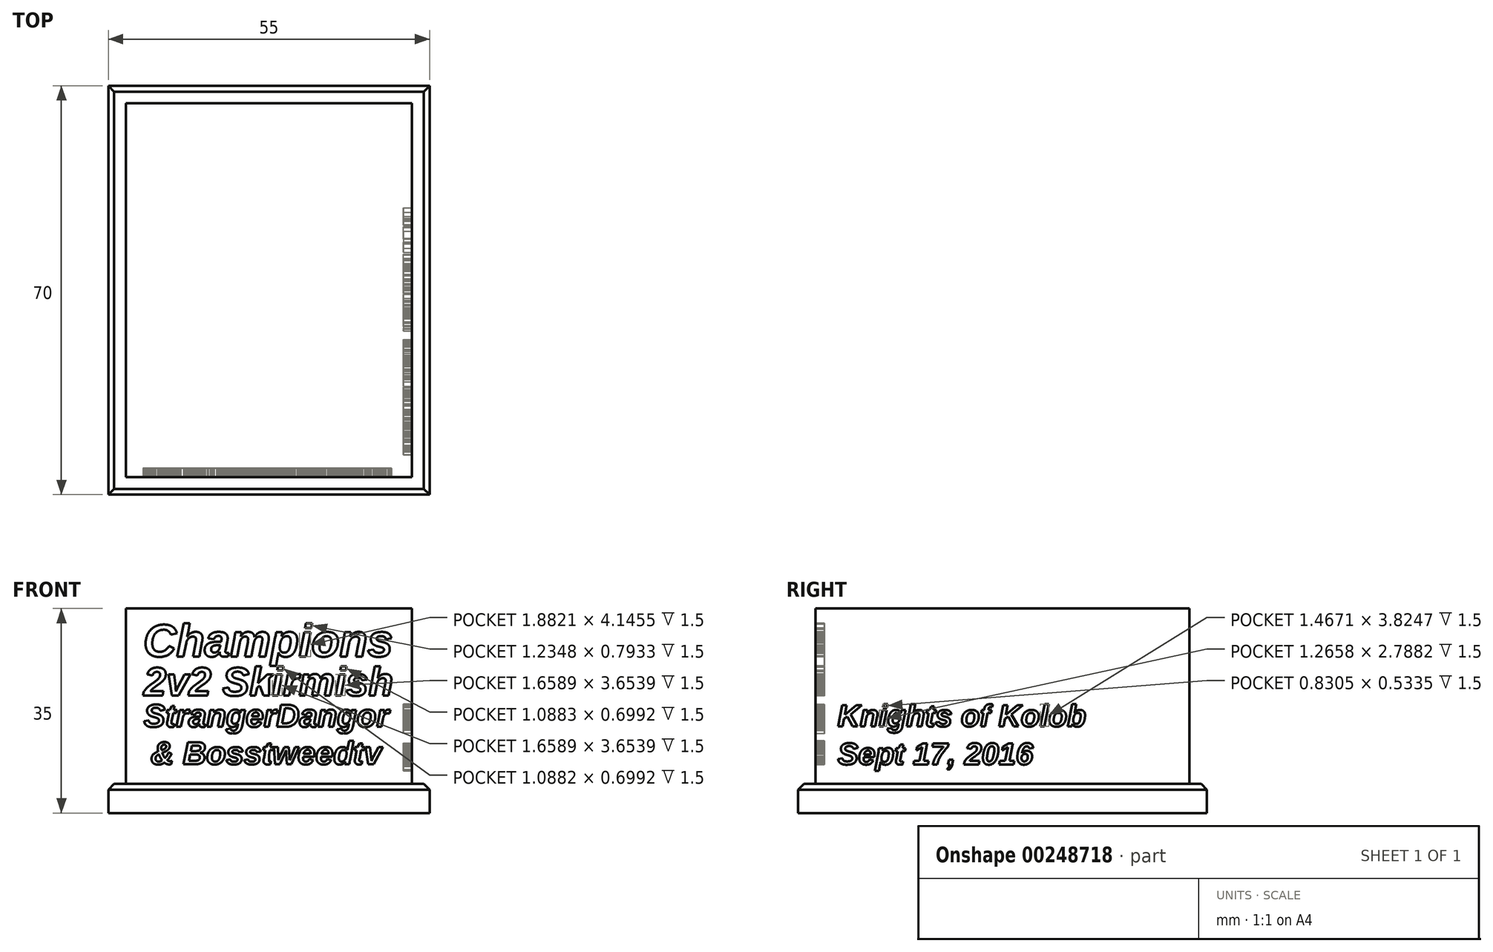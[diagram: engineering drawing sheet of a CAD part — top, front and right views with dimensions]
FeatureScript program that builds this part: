
annotation { "Feature Type Name" : "Feature", "Feature Type Description" : "" }
export const myFeature = defineFeature(function(context is Context, id is Id, definition is map)
    precondition{}
    {
        {
            var Q0;
            Q0=qCreatedBy(makeId("Top.planeOp"),FACE);
            var sketch = newSketch(context, id + "F0", { "sketchPlane" : qUnion([Q0])});
            skLineSegment(sketch, "E0.bottom", {"start": v(0, 0) * mm, "end": v(55, 0) * mm});
            skLineSegment(sketch, "E0.top", {"start": v(0, 70) * mm, "end": v(55, 70) * mm});
            skLineSegment(sketch, "E0.left", {"start": v(0, 0) * mm, "end": v(0, 70) * mm});
            skLineSegment(sketch, "E0.right", {"start": v(55, 0) * mm, "end": v(55, 70) * mm});
            skSolve(sketch);
        }
        {
            var Q0;
            Q0=makeQuery(id+"F0.imprint","IMPRINT",FACE,{"disambiguationData":[TD([[makeQuery(id+"F0.imprint","IMPRINT",EDGE,{"derivedFrom":sQuery(id+"F0.wireOp",EDGE,"E0.bottom")}),1.0]])]});
            extrude(context, id + "F1", {"entities" : qUnion([Q0]), "depth" : 5 * mm});
        }
        {
            var Q0;
            Q0=makeQuery(id+"F1.opExtrude","CAP_FACE",FACE,{"disambiguationData":[OSD([sQuery(id+"F0.wireOp",EDGE,"E0.bottom"),sQuery(id+"F0.wireOp",EDGE,"E0.top"),sQuery(id+"F0.wireOp",EDGE,"E0.left"),sQuery(id+"F0.wireOp",EDGE,"E0.right")])],"isStart":false});
            var sketch = newSketch(context, id + "F2", { "sketchPlane" : qUnion([Q0])});
            skLineSegment(sketch, "E1", {"start": v(0, 0) * mm, "end": v(3, 0) * mm});
            skLineSegment(sketch, "E2", {"start": v(3, 0) * mm, "end": v(3, 3) * mm});
            skLineSegment(sketch, "E3.bottom", {"start": v(3, 3) * mm, "end": v(52, 3) * mm});
            skLineSegment(sketch, "E3.top", {"start": v(3, 67) * mm, "end": v(52, 67) * mm});
            skLineSegment(sketch, "E3.left", {"start": v(3, 3) * mm, "end": v(3, 67) * mm});
            skLineSegment(sketch, "E3.right", {"start": v(52, 3) * mm, "end": v(52, 67) * mm});
            skSolve(sketch);
        }
        {
            var Q0;
            Q0 = qSketchRegion(id + "F2", true);
            var Q1;
            Q1=makeQuery(id+"F2.imprint","IMPRINT",FACE,{"disambiguationData":[TD([[makeQuery(id+"F2.imprint","IMPRINT",EDGE,{"derivedFrom":sQuery(id+"F2.wireOp",EDGE,"E3.bottom")}),1.0]])]});
            extrude(context, id + "F3", {"entities" : qUnion([Q0, Q1]), "operationType" : NewBodyOperationType.ADD, "depth" : 30 * mm});
        }
        {
            var Q0;
            Q0=makeQuery(id+"F3.opExtrude","SWEPT_FACE",FACE,{"disambiguationData":[OSD([sQuery(id+"F2.wireOp",EDGE,"E3.bottom")])]});
            var sketch = newSketch(context, id + "F4", { "sketchPlane" : qUnion([Q0])});
            skLineSegment(sketch, "E4", {"start": v(27.5, 35) * mm, "end": v(27.5, 5) * mm});
            skText(sketch, "E5", { "text": "StrangerDangor", "fontName": "Arimo-BoldItalic.ttf"});
            skText(sketch, "E6", { "text": "& Bosstweedtv", "fontName": "Arimo-BoldItalic.ttf"});
            skText(sketch, "E7", { "text": "Champions", "fontName": "Arimo-BoldItalic.ttf"});
            skText(sketch, "E8", { "text": "2v2 Skirmish", "fontName": "Arimo-BoldItalic.ttf"});
            const initialGuessF4  = {"E5": [0.00607, 0.01474, 1, 0, 0.00397], "E6": [0.00727, 0.00834, 1, 0, 0.00397], "E7": [0.006, 0.02679, 1, 0, 0.00565], "E8": [0.00607, 0.02008, 1, 0, 0.00498]};
            skSetInitialGuess(sketch, initialGuessF4);
            skSolve(sketch);
        }
        {
            var Q0;
            Q0=makeQuery(id+"F3.opExtrude","SWEPT_FACE",FACE,{"disambiguationData":[OSD([sQuery(id+"F2.wireOp",EDGE,"E3.right")])]});
            var sketch = newSketch(context, id + "F5", { "sketchPlane" : qUnion([Q0])});
            skText(sketch, "E9", { "text": "Sept 17, 2016", "fontName": "Arimo-BoldItalic.ttf"});
            skText(sketch, "E10", { "text": "Knights of Kolob", "fontName": "Arimo-BoldItalic.ttf"});
            const initialGuessF5  = {"E9": [0.00678, 0.00831, 1, 0, 0.0038], "E10": [0.00678, 0.01481, 1, 0, 0.0038]};
            skSetInitialGuess(sketch, initialGuessF5);
            skSolve(sketch);
        }
        {
            var Q0;
            Q0=makeQuery(id+"F1.opExtrude","CAP_EDGE",EDGE,{"disambiguationData":[OSD([sQuery(id+"F0.wireOp",EDGE,"E0.bottom")])],"isStart":false});
            var Q1;
            Q1=makeQuery(id+"F1.opExtrude","CAP_EDGE",EDGE,{"disambiguationData":[OSD([sQuery(id+"F0.wireOp",EDGE,"E0.right")])],"isStart":false});
            var Q2;
            Q2=makeQuery(id+"F1.opExtrude","CAP_EDGE",EDGE,{"disambiguationData":[OSD([sQuery(id+"F0.wireOp",EDGE,"E0.left")])],"isStart":false});
            var Q3;
            Q3=makeQuery(id+"F1.opExtrude","CAP_EDGE",EDGE,{"disambiguationData":[OSD([sQuery(id+"F0.wireOp",EDGE,"E0.top")])],"isStart":false});
            chamfer(context, id + "F6", {"entities" : qUnion([Q0, Q1, Q2, Q3]), "width" : 1 * mm, "tangentPropagation" : true});
        }
        {
            var Q0;
            Q0 = qSketchRegion(id + "F4", true);
            extrude(context, id + "F7", {"entities" : qUnion([Q0]), "operationType" : NewBodyOperationType.REMOVE, "oppositeDirection" : true, "depth" : 1.5 * mm});
        }
        {
            var Q0;
            Q0 = qSketchRegion(id + "F5", true);
            extrude(context, id + "F8", {"entities" : qUnion([Q0]), "operationType" : NewBodyOperationType.REMOVE, "oppositeDirection" : true, "depth" : 1.5 * mm});
        }
    });
